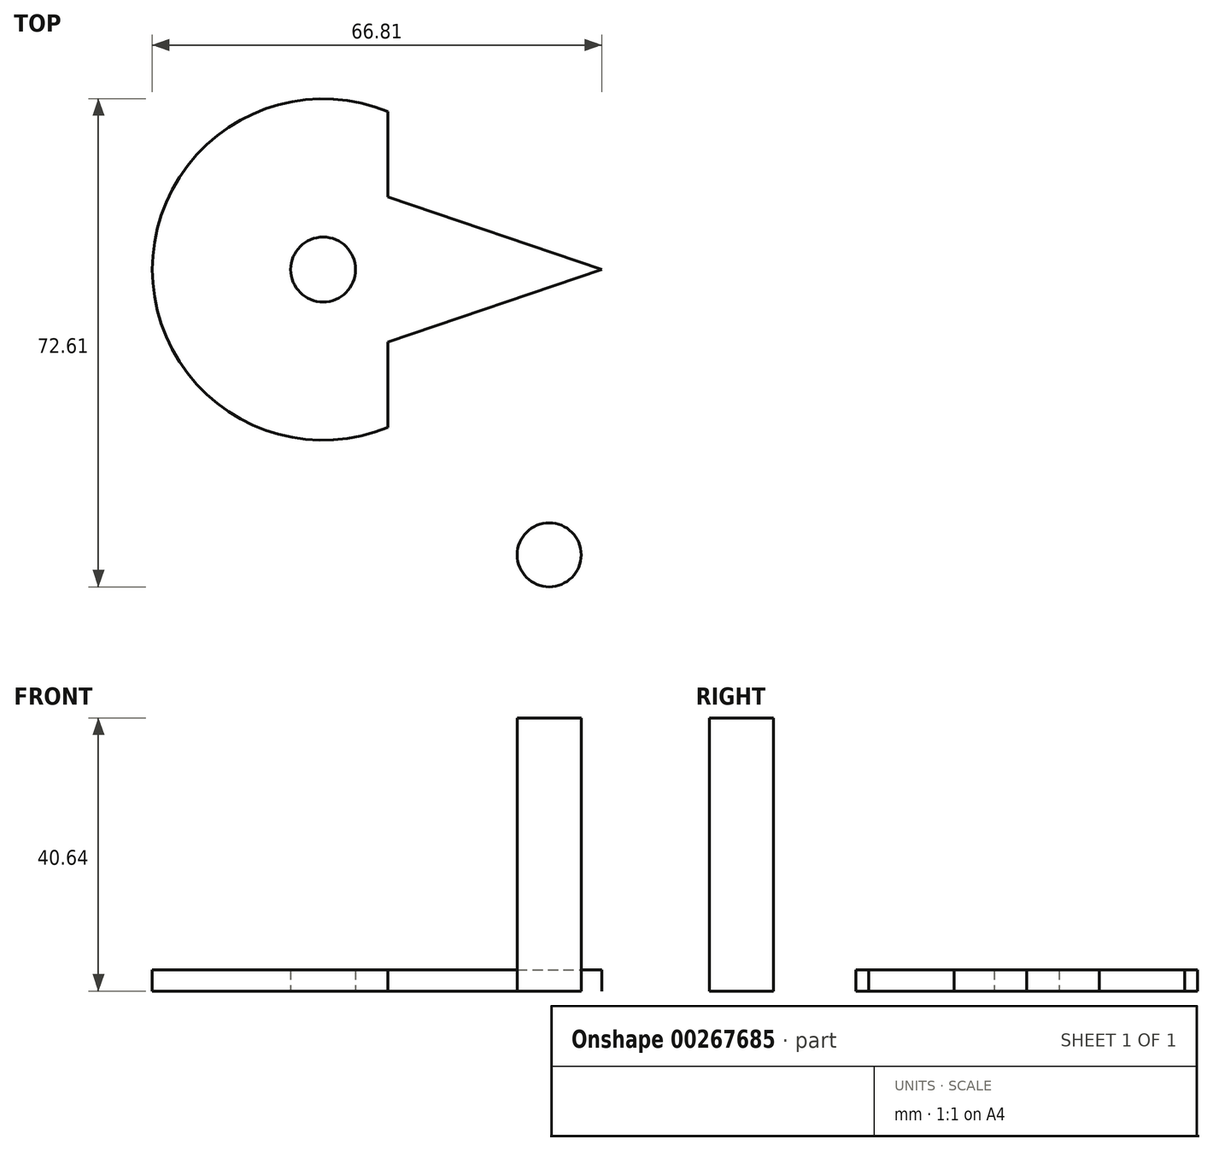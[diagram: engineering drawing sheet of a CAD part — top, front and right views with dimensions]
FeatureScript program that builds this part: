
annotation { "Feature Type Name" : "Feature", "Feature Type Description" : "" }
export const myFeature = defineFeature(function(context is Context, id is Id, definition is map)
    precondition{}
    {
        {
            var Q0;
            Q0=qCreatedBy(makeId("Top.planeOp"),FACE);
            var sketch = newSketch(context, id + "F0", { "sketchPlane" : qUnion([Q0])});
            skArc(sketch, "E0", {"start": v(9.66, 23.5) * mm, "mid": v(-25.4, 0) * mm, "end": v(9.66, -23.5) * mm});
            skCircle(sketch, "E1", {"center": v(0, 0) * mm, "radius": 4.83 * mm});
            skLineSegment(sketch, "E2", {"start": v(9.66, 23.5) * mm, "end": v(9.66, 10.8) * mm});
            skLineSegment(sketch, "E3", {"start": v(9.66, -10.8) * mm, "end": v(41.4, 0) * mm});
            skLineSegment(sketch, "E4", {"start": v(41.4, 0) * mm, "end": v(9.66, 10.8) * mm});
            skLineSegment(sketch, "E5.trimOffspring", {"start": v(9.66, -10.8) * mm, "end": v(9.66, -23.5) * mm});
            skSolve(sketch);
        }
        {
            var Q0;
            Q0=makeQuery(id+"F0.imprint","IMPRINT",FACE,{"disambiguationData":[TD([[makeQuery(id+"F0.imprint","IMPRINT",EDGE,{"derivedFrom":sQuery(id+"F0.wireOp",EDGE,"E0")}),1.0]])]});
            extrude(context, id + "F1", {"entities" : qUnion([Q0]), "depth" : 3.17 * mm});
        }
        {
            var Q0;
            Q0=qCreatedBy(makeId("Top.planeOp"),FACE);
            var sketch = newSketch(context, id + "F2", { "sketchPlane" : qUnion([Q0])});
            skCircle(sketch, "E6", {"center": v(33.6, -42.45) * mm, "radius": 4.76 * mm});
            skSolve(sketch);
        }
        {
            var Q0;
            Q0=makeQuery(id+"F2.imprint","IMPRINT",FACE,{"disambiguationData":[TD([[makeQuery(id+"F2.imprint","IMPRINT",EDGE,{"derivedFrom":sQuery(id+"F2.wireOp",EDGE,"E6")}),1.0]])]});
            extrude(context, id + "F3", {"entities" : qUnion([Q0]), "depth" : 40.64 * mm});
        }
    });
